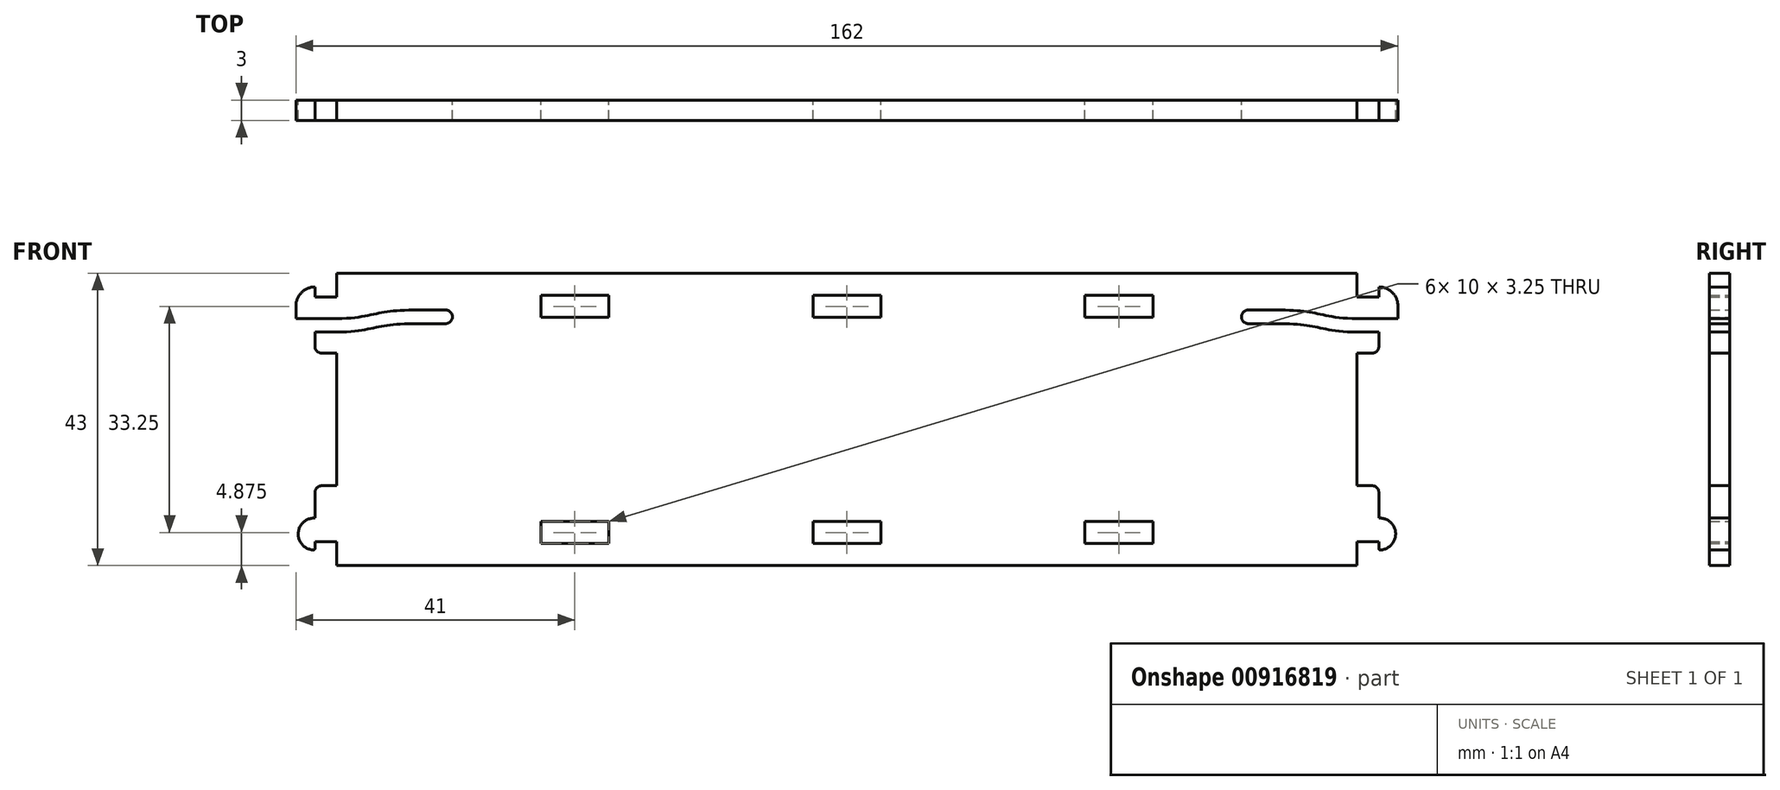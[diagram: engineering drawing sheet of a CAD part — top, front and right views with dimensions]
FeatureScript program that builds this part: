
annotation { "Feature Type Name" : "Feature", "Feature Type Description" : "" }
export const myFeature = defineFeature(function(context is Context, id is Id, definition is map)
    precondition{}
    {
        {
            var Q0;
            Q0=qCreatedBy(makeId("Front.planeOp"),FACE);
            var sketch = newSketch(context, id + "F0", { "sketchPlane" : qUnion([Q0])});
            skLineSegment(sketch, "E0.bottom", {"start": v(-75, 21.5) * mm, "end": v(75, 21.5) * mm});
            skLineSegment(sketch, "E0.top", {"start": v(-75, -21.5) * mm, "end": v(75, -21.5) * mm});
            skLineSegment(sketch, "E1.bottom", {"start": v(-45, 18.25) * mm, "end": v(-35, 18.25) * mm});
            skLineSegment(sketch, "E1.top", {"start": v(-45, 15) * mm, "end": v(-35, 15) * mm});
            skLineSegment(sketch, "E1.left", {"start": v(-45, 18.25) * mm, "end": v(-45, 15) * mm});
            skLineSegment(sketch, "E1.right", {"start": v(-35, 18.25) * mm, "end": v(-35, 15) * mm});
            skLineSegment(sketch, "E2", {"start": v(0, 21.5) * mm, "end": v(0, -21.5) * mm, "construction": true});
            skLineSegment(sketch, "E3", {"start": v(-75, 0) * mm, "end": v(75, 0) * mm, "construction": true});
            skLineSegment(sketch, "E4.MirrorCS", {"start": v(35, 18.25) * mm, "end": v(35, 15) * mm});
            skLineSegment(sketch, "E5.MirrorCS", {"start": v(45, 18.25) * mm, "end": v(35, 18.25) * mm});
            skLineSegment(sketch, "E6.MirrorCS", {"start": v(45, 15) * mm, "end": v(35, 15) * mm});
            skLineSegment(sketch, "E7.MirrorCS", {"start": v(45, 18.25) * mm, "end": v(45, 15) * mm});
            skLineSegment(sketch, "E8.MirrorCS", {"start": v(75, 0) * mm, "end": v(-75, 0) * mm, "construction": true});
            skLineSegment(sketch, "E9.MirrorCS", {"start": v(35, -18.25) * mm, "end": v(35, -15) * mm});
            skLineSegment(sketch, "E10.MirrorCS", {"start": v(45, -15) * mm, "end": v(35, -15) * mm});
            skLineSegment(sketch, "E11.MirrorCS", {"start": v(45, -18.25) * mm, "end": v(45, -15) * mm});
            skLineSegment(sketch, "E12.MirrorCS", {"start": v(45, -18.25) * mm, "end": v(35, -18.25) * mm});
            skLineSegment(sketch, "E13.MirrorCS", {"start": v(-35, -18.25) * mm, "end": v(-35, -15) * mm});
            skLineSegment(sketch, "E14.MirrorCS", {"start": v(-45, -15) * mm, "end": v(-35, -15) * mm});
            skLineSegment(sketch, "E15.MirrorCS", {"start": v(-45, -18.25) * mm, "end": v(-35, -18.25) * mm});
            skLineSegment(sketch, "E16.MirrorCS", {"start": v(-45, -18.25) * mm, "end": v(-45, -15) * mm});
            skLineSegment(sketch, "E17.bottom", {"start": v(-5, 18.25) * mm, "end": v(5, 18.25) * mm});
            skLineSegment(sketch, "E17.top", {"start": v(-5, 15) * mm, "end": v(5, 15) * mm});
            skLineSegment(sketch, "E17.left", {"start": v(-5, 18.25) * mm, "end": v(-5, 15) * mm});
            skLineSegment(sketch, "E17.right", {"start": v(5, 18.25) * mm, "end": v(5, 15) * mm});
            skLineSegment(sketch, "E18.MirrorCS", {"start": v(-5, -18.25) * mm, "end": v(5, -18.25) * mm});
            skLineSegment(sketch, "E19.MirrorCS", {"start": v(-5, -18.25) * mm, "end": v(-5, -15) * mm});
            skLineSegment(sketch, "E20.MirrorCS", {"start": v(0, -21.5) * mm, "end": v(0, 21.5) * mm, "construction": true});
            skLineSegment(sketch, "E21.MirrorCS", {"start": v(-5, -15) * mm, "end": v(5, -15) * mm});
            skLineSegment(sketch, "E22.MirrorCS", {"start": v(5, -18.25) * mm, "end": v(5, -15) * mm});
            skLineSegment(sketch, "E23.trimOffspring", {"start": v(-75, 9.75) * mm, "end": v(-75, -21.5) * mm});
            skLineSegment(sketch, "E24.right", {"start": v(-81, 16.68) * mm, "end": v(-80.99, 14.85) * mm});
            skArc(sketch, "E25.filletArc", {"start": v(-78.2, 19.5) * mm, "mid": v(-80.19, 18.67) * mm, "end": v(-81, 16.68) * mm});
            skLineSegment(sketch, "E26.left", {"start": v(-78.2, 19.5) * mm, "end": v(-78.2, 18) * mm});
            skLineSegment(sketch, "E27.bottom", {"start": v(-80.99, 14.85) * mm, "end": v(-75, 14.85) * mm});
            skFitSpline(sketch, "E28", {"points": [v(-75, 14.85) * mm, v(-69, 15.6) * mm, v(-63, 16.1) * mm], "startDerivative": vector(17.98, 0) * mm, "endDerivative": vector(18.02, 0) * mm});
            skLineSegment(sketch, "E29", {"start": v(-74.98, 16.8) * mm, "end": v(-57.36, 16.92) * mm, "construction": true});
            skFitSpline(sketch, "E30", {"points": [v(-75, 12.85) * mm, v(-69, 13.6) * mm, v(-63, 14.1) * mm], "startDerivative": vector(17.98, 0) * mm, "endDerivative": vector(18.02, 0) * mm});
            skLineSegment(sketch, "E31.MirrorCS", {"start": v(-78.2, -19.2) * mm, "end": v(-78.2, -18) * mm});
            skLineSegment(sketch, "E32.MirrorCS", {"start": v(-78.2, -18) * mm, "end": v(-75, -18) * mm});
            skLineSegment(sketch, "E33.MirrorCS", {"start": v(-75, -9.75) * mm, "end": v(-77.2, -9.75) * mm});
            skLineSegment(sketch, "E34.MirrorCS", {"start": v(-78.2, -19) * mm, "end": v(-78.2, -18) * mm});
            skPoint(sketch, "E35.MirrorCS.end.orphan", {"position": v(-74.97, -14.4) * mm});
            skPoint(sketch, "E36.MirrorCS.end.orphan", {"position": v(-74.97, -14.85) * mm});
            skPoint(sketch, "E27.top.end.orphan", {"position": v(-74.97, 14.4) * mm});
            skLineSegment(sketch, "E37.bottom", {"start": v(-75, 12.85) * mm, "end": v(-78.2, 12.85) * mm});
            skLineSegment(sketch, "E37.top", {"start": v(-75, 9.75) * mm, "end": v(-77.2, 9.75) * mm});
            skLineSegment(sketch, "E37.right", {"start": v(-78.2, 12.85) * mm, "end": v(-78.2, 10.75) * mm});
            skPoint(sketch, "E38.visualSharp", {"position": v(-78.2, 9.75) * mm});
            skArc(sketch, "E38.filletArc", {"start": v(-78.2, 10.75) * mm, "mid": v(-77.9, 10.04) * mm, "end": v(-77.2, 9.75) * mm});
            skLineSegment(sketch, "E39", {"start": v(-78.2, -12.38) * mm, "end": v(-78.2, -10.75) * mm});
            skPoint(sketch, "E40.visualSharp", {"position": v(-78.2, -9.75) * mm});
            skArc(sketch, "E40.filletArc", {"start": v(-77.2, -9.75) * mm, "mid": v(-77.9, -10.04) * mm, "end": v(-78.2, -10.75) * mm});
            skLineSegment(sketch, "E41.MirrorCS", {"start": v(75, 12.85) * mm, "end": v(78.2, 12.85) * mm});
            skArc(sketch, "E42.MirrorCS", {"start": v(78.2, 10.75) * mm, "mid": v(77.9, 10.04) * mm, "end": v(77.2, 9.75) * mm});
            skLineSegment(sketch, "E43.MirrorCS", {"start": v(75, 9.75) * mm, "end": v(77.2, 9.75) * mm});
            skLineSegment(sketch, "E44.MirrorCS", {"start": v(78.2, 18) * mm, "end": v(75, 18) * mm});
            skLineSegment(sketch, "E45.MirrorCS", {"start": v(78.2, 12.85) * mm, "end": v(78.2, 10.75) * mm});
            skArc(sketch, "E46.MirrorCS", {"start": v(78.2, 19.5) * mm, "mid": v(80.19, 18.67) * mm, "end": v(81, 16.68) * mm});
            skLineSegment(sketch, "E47.MirrorCS", {"start": v(80.99, 14.85) * mm, "end": v(74.97, 14.85) * mm});
            skLineSegment(sketch, "E48.MirrorCS", {"start": v(81, 16.68) * mm, "end": v(80.99, 14.85) * mm});
            skLineSegment(sketch, "E49.MirrorCS", {"start": v(75, 19) * mm, "end": v(75, 18) * mm});
            skLineSegment(sketch, "E50.MirrorCS", {"start": v(75, 21.5) * mm, "end": v(75, 19) * mm});
            skLineSegment(sketch, "E51.MirrorCS", {"start": v(78.2, 19.5) * mm, "end": v(78.2, 18) * mm});
            skPoint(sketch, "E52.MirrorP", {"position": v(74.97, 14.4) * mm});
            skPoint(sketch, "E53.MirrorP", {"position": v(78.2, 9.75) * mm});
            skFitSpline(sketch, "E54.MirrorCS", {"points": [v(75, 14.85) * mm, v(69, 15.6) * mm, v(63, 16.1) * mm], "startDerivative": vector(-17.98, 0) * mm, "endDerivative": vector(-18.02, 0) * mm});
            skFitSpline(sketch, "E55.MirrorCS", {"points": [v(75, 12.85) * mm, v(69, 13.6) * mm, v(63, 14.1) * mm], "startDerivative": vector(-17.98, 0) * mm, "endDerivative": vector(-18.02, 0) * mm});
            skArc(sketch, "E56", {"start": v(-78.2, -14.5) * mm, "mid": v(-80.66, -16.75) * mm, "end": v(-78.4, -19.2) * mm});
            skLineSegment(sketch, "E57", {"start": v(-78.2, -12.38) * mm, "end": v(-78.2, -14.5) * mm});
            skLineSegment(sketch, "E58.MirrorCS", {"start": v(75, 9.75) * mm, "end": v(75, -21.5) * mm});
            skLineSegment(sketch, "E59.MirrorCS", {"start": v(78.2, -18) * mm, "end": v(75, -18) * mm});
            skArc(sketch, "E60.MirrorCS", {"start": v(77.2, -9.75) * mm, "mid": v(77.9, -10.04) * mm, "end": v(78.2, -10.75) * mm});
            skLineSegment(sketch, "E61.MirrorCS", {"start": v(78.2, -19.2) * mm, "end": v(78.2, -18) * mm});
            skPoint(sketch, "E62.MirrorP", {"position": v(78.2, -9.75) * mm});
            skLineSegment(sketch, "E63.MirrorCS", {"start": v(75, -9.75) * mm, "end": v(77.2, -9.75) * mm});
            skLineSegment(sketch, "E64.MirrorCS", {"start": v(78.2, -19) * mm, "end": v(78.2, -18) * mm});
            skPoint(sketch, "E65.MirrorP", {"position": v(74.97, -14.85) * mm});
            skLineSegment(sketch, "E66.MirrorCS", {"start": v(78.2, -12.38) * mm, "end": v(78.2, -10.75) * mm});
            skLineSegment(sketch, "E67.MirrorCS", {"start": v(78.2, -12.38) * mm, "end": v(78.2, -14.5) * mm});
            skPoint(sketch, "E68.MirrorP", {"position": v(74.97, -14.4) * mm});
            skArc(sketch, "E69.MirrorCS", {"start": v(78.2, -14.5) * mm, "mid": v(80.66, -16.75) * mm, "end": v(78.4, -19.2) * mm});
            skPoint(sketch, "E70.MirrorCS.end.orphan", {"position": v(78.2, -19.2) * mm});
            skPoint(sketch, "E71.visualSharp", {"position": v(-78.2, -19.2) * mm});
            skArc(sketch, "E71.filletArc", {"start": v(-78.4, -19.2) * mm, "mid": v(-78.26, -19.15) * mm, "end": v(-78.2, -19) * mm});
            skArc(sketch, "E72.filletArc", {"start": v(78.2, -19) * mm, "mid": v(78.26, -19.15) * mm, "end": v(78.4, -19.2) * mm});
            skLineSegment(sketch, "E73.bottom", {"start": v(-63, 16.1) * mm, "end": v(-59, 16.1) * mm});
            skLineSegment(sketch, "E73.top", {"start": v(-63, 14.1) * mm, "end": v(-59, 14.1) * mm});
            skArc(sketch, "E74", {"start": v(-59, 16.1) * mm, "mid": v(-58, 15.1) * mm, "end": v(-59, 14.1) * mm});
            skLineSegment(sketch, "E75.bottom", {"start": v(63, 16.1) * mm, "end": v(59, 16.1) * mm});
            skLineSegment(sketch, "E75.top", {"start": v(63, 14.1) * mm, "end": v(59, 14.1) * mm});
            skArc(sketch, "E76", {"start": v(59, 14.1) * mm, "mid": v(58, 15.1) * mm, "end": v(59, 16.1) * mm});
            skLineSegment(sketch, "E77", {"start": v(-75, 21.5) * mm, "end": v(-75, 18) * mm});
            skLineSegment(sketch, "E78", {"start": v(-78.2, 18) * mm, "end": v(-75, 18) * mm});
            skSolve(sketch);
        }
        {
            var Q0;
            Q0 = qSketchRegion(id + "F0", true);
            extrude(context, id + "F1", {"entities" : qUnion([Q0]), "depth" : 3 * mm, "offsetDistance" : 25 * mm});
        }
    });
